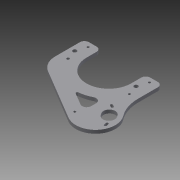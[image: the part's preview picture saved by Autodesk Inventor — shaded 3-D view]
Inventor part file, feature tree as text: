
AUTODESK INVENTOR PART (.ipt)
format: ipt  version: 2015 (Build 190159000, 159)  size: 227,328 bytes
history: native  units: mm
features: reference x14, extrude x2, sketch x2, fillet x1, projected_geometry x1
ambient origin geometry x8: Origin, YZ Plane, XZ Plane, XY Plane, X Axis, Y Axis, Z Axis, Center Point
bodies: Solid1 (feature_tree)
feature tree (20):
  extrude  "Extrusion1"  Depth=3.0mm
  extrude  "Extrusion2"  Depth=1.0mm
  fillet  "Fillet1"  Radius=12.5mm
  sketch  "Sketch1"  dims[d0=3.0mm d1=0.872665mm]
  reference  "Reference1"
  reference  "Reference2"
  reference  "Reference3"
  reference  "Reference4"
  reference  "Reference5"
  reference  "Reference6"
  reference  "Reference7"
  reference  "Reference8"
  reference  "Reference9"
  reference  "Reference10"
  reference  "Reference11"
  reference  "Reference12"
  reference  "Reference14"
  reference  "Reference15"
  sketch  "Sketch2"  dims[d2=0.872665mm d3=0.872665mm d4=12.5mm d5=3.0mm d6=4.0mm d7=4.0mm d8=5.0mm d9=4.0mm d10=5.0mm d11=4.0mm d12=4.0mm d13=3.0mm d14=0.0mm d15=4.0mm d16=3.5mm d17=2.0mm d18=10.0mm d19=0.0mm d20=2.0mm d21=2.0mm d22=2.0mm d23=3.5mm d24=1.0mm d25=1.0mm d26=0.5mm d27=0.5mm]
  projected_geometry  "Projected Loop1"
